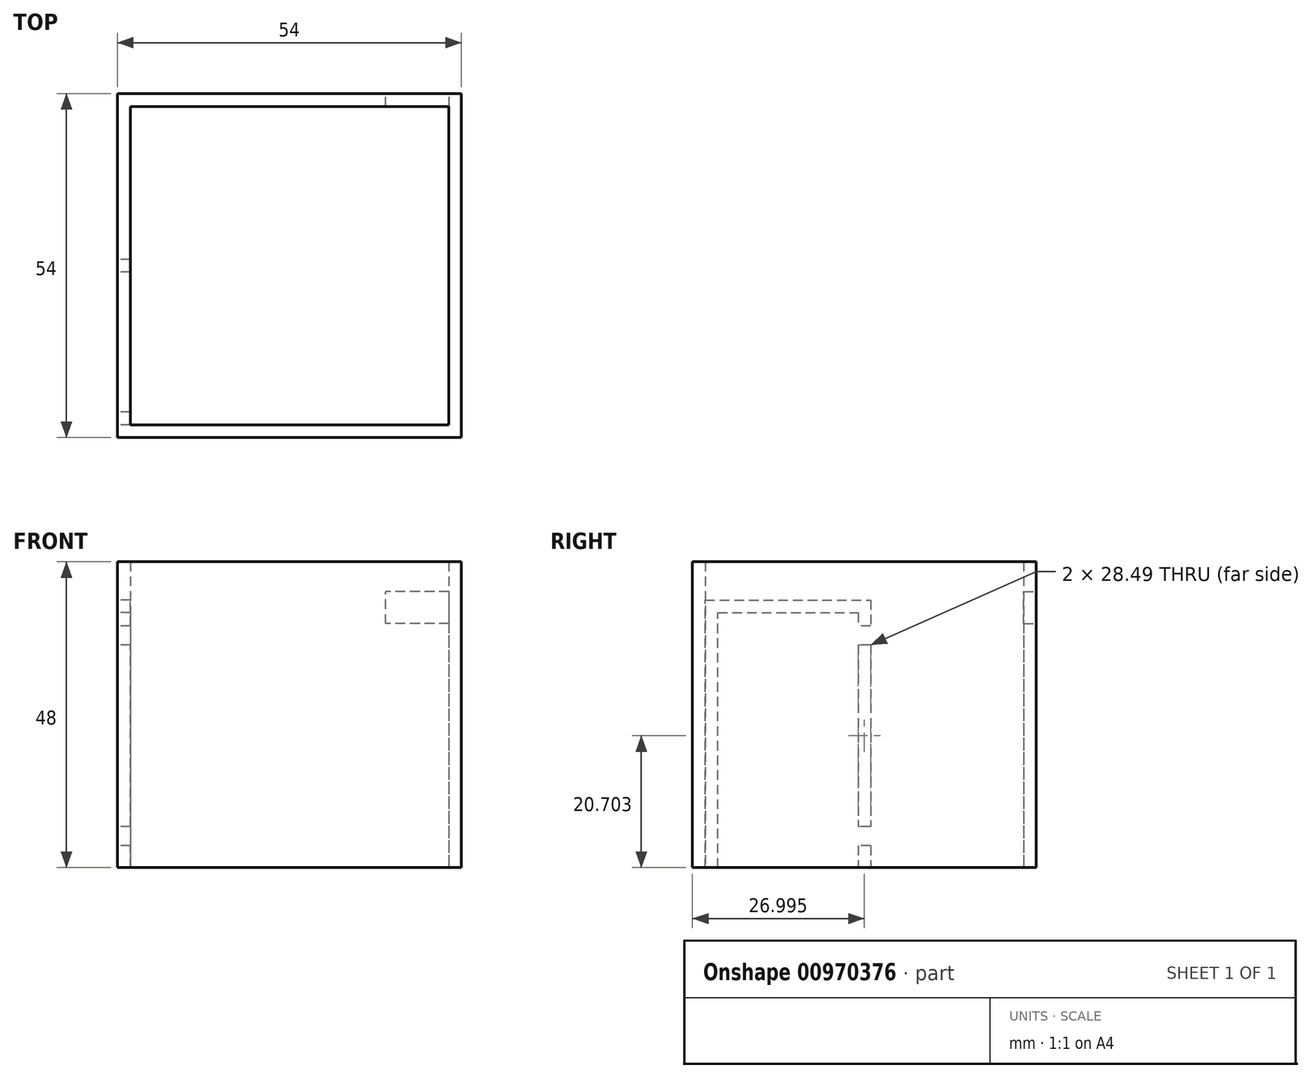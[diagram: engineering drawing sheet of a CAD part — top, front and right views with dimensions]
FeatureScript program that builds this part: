
annotation { "Feature Type Name" : "Feature", "Feature Type Description" : "" }
export const myFeature = defineFeature(function(context is Context, id is Id, definition is map)
    precondition{}
    {
        {
            var Q0;
            Q0=qCreatedBy(makeId("Top.planeOp"),FACE);
            var sketch = newSketch(context, id + "F0", { "sketchPlane" : qUnion([Q0])});
            skLineSegment(sketch, "E0.bottom", {"start": v(-25.17, -3.43) * mm, "end": v(24.83, -3.43) * mm});
            skLineSegment(sketch, "E0.top", {"start": v(-25.17, -1.43) * mm, "end": v(24.83, -1.43) * mm});
            skLineSegment(sketch, "E0.left", {"start": v(-25.17, -3.43) * mm, "end": v(-25.17, -1.43) * mm});
            skLineSegment(sketch, "E0.right", {"start": v(24.83, -3.43) * mm, "end": v(24.83, -1.43) * mm});
            skPoint(sketch, "E0.middle", {"position": v(-0.17, -2.43) * mm});
            skLineSegment(sketch, "E1.bottom", {"start": v(24.83, -3.43) * mm, "end": v(26.83, -3.43) * mm});
            skLineSegment(sketch, "E1.top", {"start": v(24.83, 50.57) * mm, "end": v(26.83, 50.57) * mm});
            skLineSegment(sketch, "E1.left", {"start": v(24.83, -3.43) * mm, "end": v(24.83, 50.57) * mm});
            skLineSegment(sketch, "E1.right", {"start": v(26.83, -3.43) * mm, "end": v(26.83, 50.57) * mm});
            skLineSegment(sketch, "E2.bottom", {"start": v(24.83, 50.57) * mm, "end": v(-25.17, 50.57) * mm});
            skLineSegment(sketch, "E2.top", {"start": v(24.83, 48.57) * mm, "end": v(-25.17, 48.57) * mm});
            skLineSegment(sketch, "E2.left", {"start": v(24.83, 50.57) * mm, "end": v(24.83, 48.57) * mm});
            skLineSegment(sketch, "E2.right", {"start": v(-25.17, 50.57) * mm, "end": v(-25.17, 48.57) * mm});
            skLineSegment(sketch, "E3.bottom", {"start": v(-25.17, 50.57) * mm, "end": v(-27.17, 50.57) * mm});
            skLineSegment(sketch, "E3.top", {"start": v(-25.17, -3.43) * mm, "end": v(-27.17, -3.43) * mm});
            skLineSegment(sketch, "E3.left", {"start": v(-25.17, 50.57) * mm, "end": v(-25.17, -3.43) * mm});
            skLineSegment(sketch, "E3.right", {"start": v(-27.17, 50.57) * mm, "end": v(-27.17, -3.43) * mm});
            skSolve(sketch);
        }
        {
            var Q0;
            Q0 = qSketchRegion(id + "F0", true);
            extrude(context, id + "F1", {"entities" : qUnion([Q0]), "depth" : 48 * mm, "offsetDistance" : 25 * mm});
        }
        {
            var Q0;
            Q0=makeQuery(id+"F1.opExtrude","CAP_FACE",FACE,{"disambiguationData":[OSD([sQuery(id+"F0.wireOp",EDGE,"E0.bottom"),sQuery(id+"F0.wireOp",EDGE,"E0.top"),sQuery(id+"F0.wireOp",EDGE,"E1.bottom"),sQuery(id+"F0.wireOp",EDGE,"E1.top"),sQuery(id+"F0.wireOp",EDGE,"E1.left"),sQuery(id+"F0.wireOp",EDGE,"E1.right"),sQuery(id+"F0.wireOp",EDGE,"E2.bottom"),sQuery(id+"F0.wireOp",EDGE,"E2.top"),sQuery(id+"F0.wireOp",EDGE,"E3.bottom"),sQuery(id+"F0.wireOp",EDGE,"E3.top"),sQuery(id+"F0.wireOp",EDGE,"E3.left"),sQuery(id+"F0.wireOp",EDGE,"E3.right")])],"isStart":false});
            var sketch = newSketch(context, id + "F2", { "sketchPlane" : qUnion([Q0])});
            skLineSegment(sketch, "E4.bottom", {"start": v(26.83, 50.57) * mm, "end": v(-27.17, 50.57) * mm});
            skLineSegment(sketch, "E4.top", {"start": v(26.83, -3.43) * mm, "end": v(-27.17, -3.43) * mm});
            skLineSegment(sketch, "E4.left", {"start": v(26.83, 50.57) * mm, "end": v(26.83, -3.43) * mm});
            skLineSegment(sketch, "E4.right", {"start": v(-27.17, 50.57) * mm, "end": v(-27.17, -3.43) * mm});
            skSolve(sketch);
        }
        {
            var Q0;
            Q0=makeQuery(id+"FF2F0lytLxk9Gzw_1.boolean.opBoolean","MERGE",FACE,{"derivedFrom":[makeQuery(id+"F1.opExtrude","SWEPT_FACE",FACE,{"disambiguationData":[OSD([sQuery(id+"F0.wireOp",EDGE,"E3.right")])]}),makeQuery(id+"FF2F0lytLxk9Gzw_1.opExtrude","SWEPT_FACE",FACE,{"disambiguationData":[OSD([sQuery(id+"F2.wireOp",EDGE,"E4.right")])]})]});
            var sketch = newSketch(context, id + "F3", { "sketchPlane" : qUnion([Q0])});
            skLineSegment(sketch, "E5", {"start": v(3.43, 0) * mm, "end": v(1.43, 0) * mm, "construction": true});
            skLineSegment(sketch, "E6.bottom", {"start": v(1.43, 0) * mm, "end": v(-0.57, 0) * mm});
            skLineSegment(sketch, "E6.top", {"start": v(1.43, 40) * mm, "end": v(-0.57, 40) * mm});
            skLineSegment(sketch, "E6.left", {"start": v(1.43, 0) * mm, "end": v(1.43, 40) * mm});
            skLineSegment(sketch, "E6.right", {"start": v(-0.57, 0) * mm, "end": v(-0.57, 40) * mm});
            skLineSegment(sketch, "E7.bottom", {"start": v(1.43, 40) * mm, "end": v(-24.57, 40) * mm});
            skLineSegment(sketch, "E7.top", {"start": v(1.43, 42) * mm, "end": v(-24.57, 42) * mm});
            skLineSegment(sketch, "E7.left", {"start": v(1.43, 40) * mm, "end": v(1.43, 42) * mm});
            skLineSegment(sketch, "E7.right", {"start": v(-24.57, 40) * mm, "end": v(-24.57, 42) * mm});
            skLineSegment(sketch, "E8.bottom", {"start": v(-24.57, 40) * mm, "end": v(-22.57, 40) * mm});
            skLineSegment(sketch, "E8.top", {"start": v(-24.57, 0) * mm, "end": v(-22.57, 0) * mm});
            skLineSegment(sketch, "E8.left", {"start": v(-24.57, 40) * mm, "end": v(-24.57, 0) * mm});
            skLineSegment(sketch, "E8.right", {"start": v(-22.57, 40) * mm, "end": v(-22.57, 0) * mm});
            skLineSegment(sketch, "E9.bottom", {"start": v(-24.57, 37.95) * mm, "end": v(-22.57, 37.95) * mm});
            skLineSegment(sketch, "E9.top", {"start": v(-24.57, 34.95) * mm, "end": v(-22.57, 34.95) * mm});
            skLineSegment(sketch, "E9.left", {"start": v(-24.57, 37.95) * mm, "end": v(-24.57, 34.95) * mm});
            skLineSegment(sketch, "E9.right", {"start": v(-22.57, 37.95) * mm, "end": v(-22.57, 34.95) * mm});
            skLineSegment(sketch, "E10.bottom", {"start": v(-24.57, 3.46) * mm, "end": v(-22.57, 3.46) * mm});
            skLineSegment(sketch, "E10.top", {"start": v(-24.57, 6.46) * mm, "end": v(-22.57, 6.46) * mm});
            skLineSegment(sketch, "E10.left", {"start": v(-24.57, 3.46) * mm, "end": v(-24.57, 6.46) * mm});
            skLineSegment(sketch, "E10.right", {"start": v(-22.57, 3.46) * mm, "end": v(-22.57, 6.46) * mm});
            skSolve(sketch);
        }
        {
            var Q0;
            Q0=makeQuery(id+"F3.imprint","IMPRINT",FACE,{"disambiguationData":[TD([[makeQuery(id+"F3.imprint","IMPRINT",EDGE,{"derivedFrom":sQuery(id+"F3.wireOp",EDGE,"E6.bottom")}),1.0]])]});
            var Q1;
            {var subQ0=sQuery(id+"F3.wireOp",EDGE,"E8.top");Q1=makeQuery(id+"F3.imprint","IMPRINT",FACE,{"disambiguationData":[TD([[makeQuery(id+"F3.imprint","IMPRINT",EDGE,{"derivedFrom":subQ0}),1.0]])]});}
            var Q2;
            {var subQ0=sQuery(id+"F3.wireOp",EDGE,"E9.top");Q2=makeQuery(id+"F3.imprint","IMPRINT",FACE,{"disambiguationData":[TD([[makeQuery(id+"F3.imprint","IMPRINT",EDGE,{"derivedFrom":subQ0}),-1.0]])]});}
            var Q3;
            {var subQ5=sQuery(id+"F3.wireOp",EDGE,"E9.bottom");Q3=makeQuery(id+"F3.imprint","IMPRINT",FACE,{"disambiguationData":[TD([[makeQuery(id+"F3.imprint","IMPRINT",EDGE,{"derivedFrom":subQ5}),1.0]])]});}
            var Q4;
            {var subQ3=sQuery(id+"F3.wireOp",EDGE,"E6.top");Q4=makeQuery(id+"F3.imprint","IMPRINT",FACE,{"disambiguationData":[TD([[makeQuery(id+"F3.imprint","IMPRINT",EDGE,{"derivedFrom":subQ3}),-1.0]])]});}
            extrude(context, id + "F4", {"entities" : qUnion([Q0, Q1, Q2, Q3, Q4]), "operationType" : NewBodyOperationType.REMOVE, "oppositeDirection" : true, "depth" : 25 * mm, "offsetDistance" : 25 * mm});
        }
        {
            var Q0;
            Q0=makeQuery(id+"FF2F0lytLxk9Gzw_1.boolean.opBoolean","MERGE",FACE,{"derivedFrom":[makeQuery(id+"F1.opExtrude","SWEPT_FACE",FACE,{"disambiguationData":[OSD([sQuery(id+"F0.wireOp",EDGE,"E1.top"),sQuery(id+"F0.wireOp",EDGE,"E2.bottom"),sQuery(id+"F0.wireOp",EDGE,"E3.bottom")])]}),makeQuery(id+"FF2F0lytLxk9Gzw_1.opExtrude","SWEPT_FACE",FACE,{"disambiguationData":[OSD([sQuery(id+"F2.wireOp",EDGE,"E4.bottom")])]})]});
            var sketch = newSketch(context, id + "F5", { "sketchPlane" : qUnion([Q0])});
            skLineSegment(sketch, "E11.bottom", {"start": v(-24.9, 38.3) * mm, "end": v(-14.9, 38.3) * mm});
            skLineSegment(sketch, "E11.top", {"start": v(-24.9, 43.3) * mm, "end": v(-14.9, 43.3) * mm});
            skLineSegment(sketch, "E11.left", {"start": v(-24.9, 38.3) * mm, "end": v(-24.9, 43.3) * mm});
            skLineSegment(sketch, "E11.right", {"start": v(-14.9, 38.3) * mm, "end": v(-14.9, 43.3) * mm});
            skSolve(sketch);
        }
        {
            var Q0;
            Q0 = qSketchRegion(id + "F5", true);
            var Q1;
            Q1=makeQuery(id+"F5.imprint","IMPRINT",FACE,{"disambiguationData":[TD([[makeQuery(id+"F5.imprint","IMPRINT",EDGE,{"derivedFrom":sQuery(id+"F5.wireOp",EDGE,"E11.bottom")}),1.0]])]});
            extrude(context, id + "F6", {"entities" : qUnion([Q0, Q1]), "operationType" : NewBodyOperationType.REMOVE, "oppositeDirection" : true, "depth" : 2 * mm, "offsetDistance" : 25 * mm});
        }
    });
